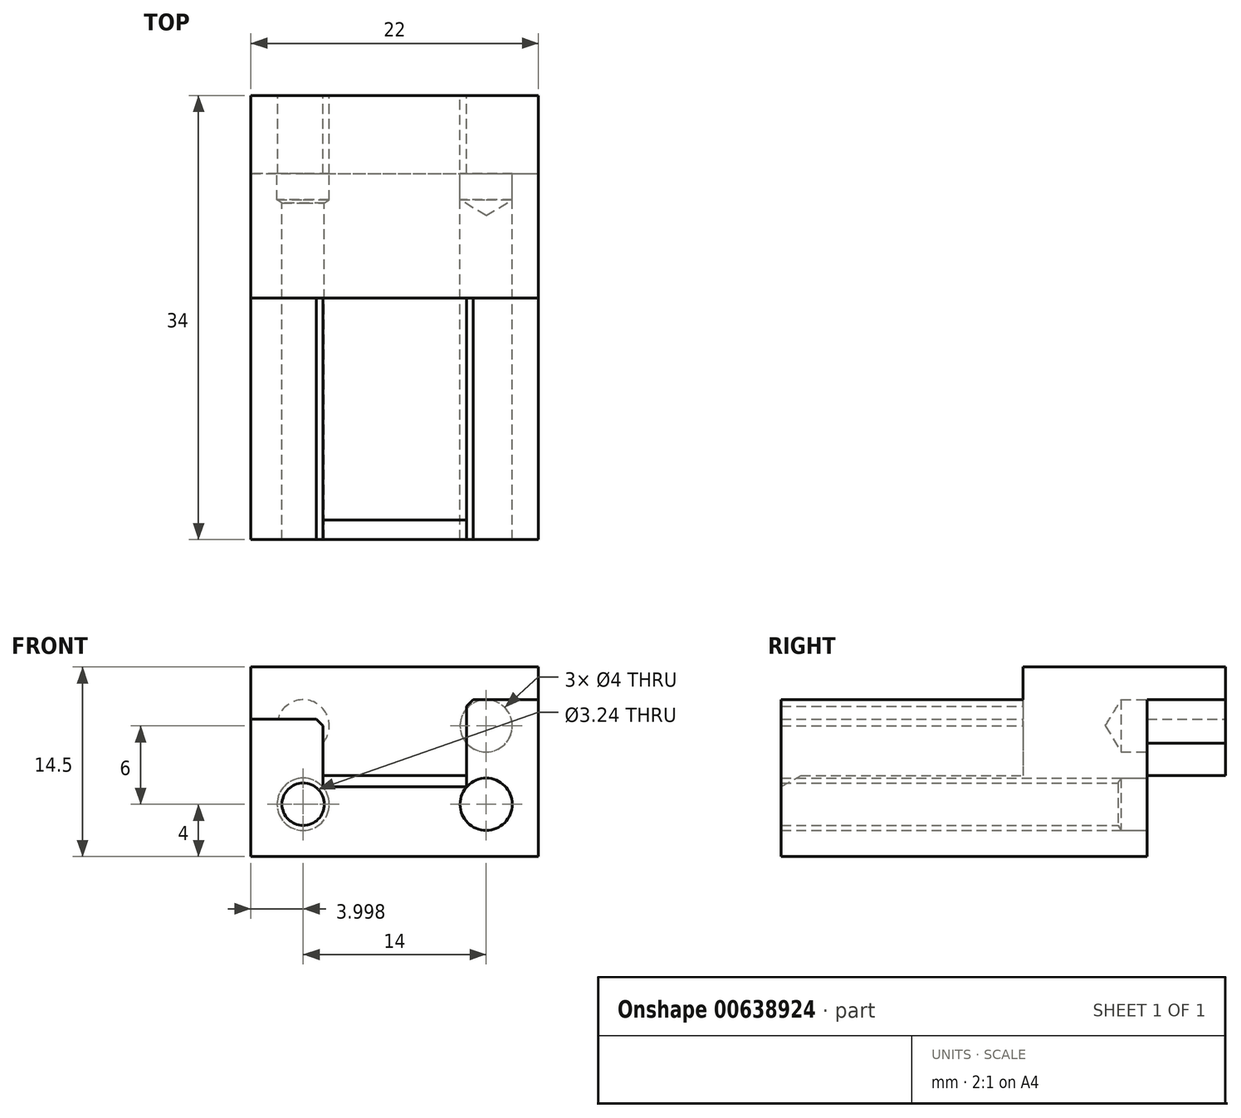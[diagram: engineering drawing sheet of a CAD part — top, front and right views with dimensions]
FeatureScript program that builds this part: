
annotation { "Feature Type Name" : "Feature", "Feature Type Description" : "" }
export const myFeature = defineFeature(function(context is Context, id is Id, definition is map)
    precondition{}
    {
        {
            var Q0;
            Q0=qCreatedBy(makeId("Front.planeOp"),FACE);
            var sketch = newSketch(context, id + "F0", { "sketchPlane" : qUnion([Q0])});
            skLineSegment(sketch, "E0", {"start": v(-38.92, -1.05) * mm, "end": v(-27.92, -1.05) * mm});
            skLineSegment(sketch, "E1", {"start": v(-44.42, 7.25) * mm, "end": v(-44.42, -7.25) * mm});
            skLineSegment(sketch, "E2", {"start": v(-27.92, 4.25) * mm, "end": v(-27.42, 4.75) * mm});
            skLineSegment(sketch, "E3", {"start": v(-38.92, 0.45) * mm, "end": v(-27.92, 0.45) * mm});
            skLineSegment(sketch, "E4", {"start": v(-39.42, 3.25) * mm, "end": v(-44.42, 3.25) * mm});
            skLineSegment(sketch, "E5", {"start": v(-38.92, 2.75) * mm, "end": v(-39.42, 3.25) * mm});
            skLineSegment(sketch, "E6", {"start": v(-27.92, 4.25) * mm, "end": v(-27.92, -1.05) * mm});
            skLineSegment(sketch, "E7", {"start": v(-38.92, 2.75) * mm, "end": v(-38.92, -1.05) * mm});
            skCircle(sketch, "E8", {"center": v(-26.42, 2.75) * mm, "radius": 1.62 * mm});
            skArc(sketch, "E9", {"start": v(-28.35, 2.23) * mm, "mid": v(-24.7, 1.75) * mm, "end": v(-26.94, 4.68) * mm});
            skCircle(sketch, "E10", {"center": v(-26.42, -3.25) * mm, "radius": 2 * mm});
            skLineSegment(sketch, "E11", {"start": v(-44.42, -7.25) * mm, "end": v(-22.42, -7.25) * mm});
            skLineSegment(sketch, "E12", {"start": v(-27.42, 4.75) * mm, "end": v(-22.42, 4.75) * mm});
            skLineSegment(sketch, "E13", {"start": v(-22.42, 7.25) * mm, "end": v(-44.42, 7.25) * mm});
            skLineSegment(sketch, "E14", {"start": v(-22.42, 7.25) * mm, "end": v(-22.42, -7.25) * mm});
            skCircle(sketch, "E15", {"center": v(-40.42, -3.25) * mm, "radius": 1.62 * mm});
            skArc(sketch, "E16", {"start": v(-39.9, -1.32) * mm, "mid": v(-42.15, -4.25) * mm, "end": v(-38.5, -3.77) * mm});
            skCircle(sketch, "E17", {"center": v(-40.42, 2.75) * mm, "radius": 2 * mm});
            skLineSegment(sketch, "E18", {"start": v(9.33, -1.05) * mm, "end": v(11.93, 0.45) * mm});
            skLineSegment(sketch, "E19", {"start": v(9.33, 3.25) * mm, "end": v(9.33, -7.25) * mm});
            skLineSegment(sketch, "E20", {"start": v(27.83, 7.25) * mm, "end": v(43.33, 7.25) * mm});
            skLineSegment(sketch, "E21", {"start": v(27.83, 7.25) * mm, "end": v(27.83, 0.45) * mm});
            skLineSegment(sketch, "E22", {"start": v(35.46, 2.75) * mm, "end": v(44.04, 2.75) * mm});
            skLineSegment(sketch, "E23", {"start": v(37.33, 4.75) * mm, "end": v(36.17, 2.75) * mm});
            skLineSegment(sketch, "E24", {"start": v(37.33, 0.75) * mm, "end": v(36.17, 2.75) * mm});
            skLineSegment(sketch, "E25", {"start": v(37.33, 0.75) * mm, "end": v(43.33, 0.75) * mm});
            skLineSegment(sketch, "E26", {"start": v(37.33, 4.75) * mm, "end": v(37.33, 0.75) * mm});
            skLineSegment(sketch, "E27", {"start": v(43.33, 4.75) * mm, "end": v(37.33, 4.75) * mm});
            skLineSegment(sketch, "E28", {"start": v(31.3, -3.25) * mm, "end": v(44.42, -3.25) * mm});
            skLineSegment(sketch, "E29", {"start": v(35.33, -1.25) * mm, "end": v(34.67, -1.63) * mm});
            skLineSegment(sketch, "E30", {"start": v(35.33, -5.25) * mm, "end": v(34.67, -4.87) * mm});
            skLineSegment(sketch, "E31", {"start": v(43.33, -1.25) * mm, "end": v(35.33, -1.25) * mm});
            skLineSegment(sketch, "E32", {"start": v(35.33, -5.25) * mm, "end": v(43.33, -5.25) * mm});
            skLineSegment(sketch, "E33", {"start": v(35.33, -1.25) * mm, "end": v(35.33, -5.25) * mm});
            skLineSegment(sketch, "E34", {"start": v(33.33, -1.63) * mm, "end": v(32.4, -3.25) * mm});
            skLineSegment(sketch, "E35", {"start": v(33.33, -4.87) * mm, "end": v(32.4, -3.25) * mm});
            skLineSegment(sketch, "E36", {"start": v(33.33, -4.87) * mm, "end": v(43.33, -4.87) * mm});
            skLineSegment(sketch, "E37", {"start": v(33.33, -1.63) * mm, "end": v(33.33, -4.87) * mm});
            skLineSegment(sketch, "E38", {"start": v(43.33, -1.63) * mm, "end": v(33.33, -1.63) * mm});
            skLineSegment(sketch, "E39", {"start": v(9.33, -7.25) * mm, "end": v(43.33, -7.25) * mm});
            skLineSegment(sketch, "E40", {"start": v(11.93, 0.45) * mm, "end": v(27.83, 0.45) * mm});
            skLineSegment(sketch, "E41", {"start": v(9.33, 3.25) * mm, "end": v(27.83, 3.25) * mm});
            skLineSegment(sketch, "E42", {"start": v(43.33, -7.25) * mm, "end": v(43.33, 7.25) * mm});
            skSolve(sketch);
        }
        {
            var Q0;
            {var subQ0=sQuery(id+"F0.wireOp",EDGE,"E0");Q0=makeQuery(id+"F0.imprint","IMPRINT",FACE,{"disambiguationData":[TD([[makeQuery(id+"F0.imprint","IMPRINT",EDGE,{"derivedFrom":subQ0}),1.0]])]});}
            var Q1;
            {var subQ0=sQuery(id+"F0.wireOp",EDGE,"E5");Q1=makeQuery(id+"F0.imprint","IMPRINT",FACE,{"disambiguationData":[TD([[makeQuery(id+"F0.imprint","IMPRINT",EDGE,{"derivedFrom":subQ0}),1.0]])]});}
            var Q2;
            {var subQ8=sQuery(id+"F0.wireOp",EDGE,"E2");Q2=makeQuery(id+"F0.imprint","IMPRINT",FACE,{"disambiguationData":[TD([[makeQuery(id+"F0.imprint","IMPRINT",EDGE,{"derivedFrom":subQ8}),1.0]])]});}
            var Q3;
            {var subQ0=sQuery(id+"F0.wireOp",EDGE,"E5");Q3=makeQuery(id+"F0.imprint","IMPRINT",FACE,{"disambiguationData":[TD([[makeQuery(id+"F0.imprint","IMPRINT",EDGE,{"derivedFrom":subQ0}),-1.0]])]});}
            var Q4;
            {var subQ0=sQuery(id+"F0.wireOp",EDGE,"E8");var subQ1=sQuery(id+"F0.wireOp",EDGE,"E6");var subQ2=makeQuery(id+"F0.imprint","INTERSECT",VERTEX,{"disambiguationData":[OD(0.0)],"derivedFrom":[subQ1,subQ0]});Q4=makeQuery(id+"F0.imprint","IMPRINT",FACE,{"disambiguationData":[TD([[makeQuery(id+"F0.imprint","IMPRINT",EDGE,{"disambiguationData":[TD([[subQ2,-1.0]])],"derivedFrom":subQ1}),1.0]])]});}
            var Q5;
            {var subQ7=sQuery(id+"F0.wireOp",EDGE,"E0");Q5=makeQuery(id+"F0.imprint","IMPRINT",FACE,{"disambiguationData":[TD([[makeQuery(id+"F0.imprint","IMPRINT",EDGE,{"derivedFrom":subQ7}),-1.0]])]});}
            var Q6;
            Q6=makeQuery(id+"F0.imprint","IMPRINT",FACE,{"disambiguationData":[TD([[makeQuery(id+"F0.imprint","IMPRINT",EDGE,{"derivedFrom":sQuery(id+"F0.wireOp",EDGE,"E10")}),-1.0]])]});
            var Q7;
            Q7=makeQuery(id+"F0.imprint","IMPRINT",FACE,{"disambiguationData":[TD([[makeQuery(id+"F0.imprint","IMPRINT",EDGE,{"derivedFrom":sQuery(id+"F0.wireOp",EDGE,"E15")}),-1.0]])]});
            var Q8;
            {var subQ7=sQuery(id+"F0.wireOp",EDGE,"E2");Q8=makeQuery(id+"F0.imprint","IMPRINT",FACE,{"disambiguationData":[TD([[makeQuery(id+"F0.imprint","IMPRINT",EDGE,{"derivedFrom":subQ7}),-1.0]])]});}
            var Q9;
            {var subQ0=sQuery(id+"F0.wireOp",EDGE,"E8");var subQ1=sQuery(id+"F0.wireOp",EDGE,"E6");var subQ2=makeQuery(id+"F0.imprint","INTERSECT",VERTEX,{"disambiguationData":[OD(0.0)],"derivedFrom":[subQ1,subQ0]});Q9=makeQuery(id+"F0.imprint","IMPRINT",FACE,{"disambiguationData":[TD([[makeQuery(id+"F0.imprint","IMPRINT",EDGE,{"disambiguationData":[TD([[subQ2,-1.0]])],"derivedFrom":subQ1}),-1.0]])]});}
            extrude(context, id + "F1", {"entities" : qUnion([Q0, Q1, Q2, Q3, Q4, Q5, Q6, Q7, Q8, Q9]), "depth" : 15.5 * mm, "offsetDistance" : 25 * mm});
        }
        {
            var Q0;
            Q0=makeQuery(id+"F1.opExtrude","CAP_FACE",FACE,{"disambiguationData":[OSD([sQuery(id+"F0.wireOp",EDGE,"E1"),sQuery(id+"F0.wireOp",EDGE,"E11"),sQuery(id+"F0.wireOp",EDGE,"E13"),sQuery(id+"F0.wireOp",EDGE,"E14")])],"isStart":false});
            var sketch = newSketch(context, id + "F2", { "sketchPlane" : qUnion([Q0])});
            skLineSegment(sketch, "E43.0", {"start": v(-38.92, -1.05) * mm, "end": v(-27.92, -1.05) * mm});
            skPoint(sketch, "E44.0", {"position": v(-39.17, 3) * mm});
            skLineSegment(sketch, "E45.0", {"start": v(-39.42, 3.25) * mm, "end": v(-44.42, 3.25) * mm});
            skLineSegment(sketch, "E46.0", {"start": v(-38.92, 2.75) * mm, "end": v(-39.42, 3.25) * mm});
            skLineSegment(sketch, "E47.0", {"start": v(-38.92, 2.75) * mm, "end": v(-38.92, -1.05) * mm});
            skLineSegment(sketch, "E48.0", {"start": v(-27.92, 4.25) * mm, "end": v(-27.92, -1.05) * mm});
            skLineSegment(sketch, "E49.0", {"start": v(-27.92, 4.25) * mm, "end": v(-27.42, 4.75) * mm});
            skLineSegment(sketch, "E50.0", {"start": v(-27.42, 4.75) * mm, "end": v(-22.42, 4.75) * mm});
            skLineSegment(sketch, "E51.0", {"start": v(-22.42, 7.25) * mm, "end": v(-22.42, -7.25) * mm});
            skLineSegment(sketch, "E52.0", {"start": v(-44.42, 7.25) * mm, "end": v(-44.42, -7.25) * mm});
            skLineSegment(sketch, "E53.0", {"start": v(-44.42, -7.25) * mm, "end": v(-22.42, -7.25) * mm});
            skSolve(sketch);
        }
        {
            var Q0;
            Q0=makeQuery(id+"F2.imprint","IMPRINT",FACE,{"disambiguationData":[TD([[makeQuery(id+"F2.imprint","IMPRINT",EDGE,{"derivedFrom":sQuery(id+"F2.wireOp",EDGE,"E43.0")}),-1.0]])]});
            extrude(context, id + "F3", {"entities" : qUnion([Q0]), "operationType" : NewBodyOperationType.ADD, "depth" : 18.5 * mm, "offsetDistance" : 25 * mm});
        }
        {
            var Q0;
            Q0=sQuery(id+"F0.wireOp",VERTEX,"E15.center");
            var Q1;
            Q1=sQuery(id+"F0.wireOp",VERTEX,"E8.center");
            var Q2;
            Q2=makeQuery(id+"F1.opExtrude","SWEPT_BODY",BODY,{"disambiguationData":[OSD([sQuery(id+"F0.wireOp",EDGE,"E1"),sQuery(id+"F0.wireOp",EDGE,"E11"),sQuery(id+"F0.wireOp",EDGE,"E13"),sQuery(id+"F0.wireOp",EDGE,"E14")])]});
            hole(context, id + "F4", {"style" : HoleStyle.SIMPLE, "endStyle" : HoleEndStyle.BLIND, "oppositeDirection" : true, "holeDiameter" : 4 * mm, "majorDiameter" : 5 * mm, "holeDepth" : 8 * mm, "isTappedThrough" : true, "tappedDepth" : 12 * mm, "tapClearance" : 3, "locations" : qUnion([Q0, Q1]), "scope" : qUnion([Q2])});
        }
        {
            var Q0;
            {var subQ0=sQuery(id+"F0.wireOp",EDGE,"E5");Q0=makeQuery(id+"F0.imprint","IMPRINT",FACE,{"disambiguationData":[TD([[makeQuery(id+"F0.imprint","IMPRINT",EDGE,{"derivedFrom":subQ0}),-1.0]])]});}
            var Q1;
            {var subQ0=sQuery(id+"F0.wireOp",EDGE,"E5");Q1=makeQuery(id+"F0.imprint","IMPRINT",FACE,{"disambiguationData":[TD([[makeQuery(id+"F0.imprint","IMPRINT",EDGE,{"derivedFrom":subQ0}),1.0]])]});}
            var Q2;
            Q2=makeQuery(id+"F0.imprint","IMPRINT",FACE,{"disambiguationData":[TD([[makeQuery(id+"F0.imprint","IMPRINT",EDGE,{"derivedFrom":sQuery(id+"F0.wireOp",EDGE,"E10")}),-1.0]])]});
            extrude(context, id + "F5", {"entities" : qUnion([Q0, Q1, Q2]), "operationType" : NewBodyOperationType.REMOVE, "depth" : 6 * mm, "offsetDistance" : 25 * mm});
        }
        {
            var Q0;
            Q0=makeQuery(id+"F3.opExtrude","CAP_EDGE",EDGE,{"disambiguationData":[OSD([sQuery(id+"F2.wireOp",EDGE,"E43.0")])],"isStart":false});
            chamfer(context, id + "F6", {"entities" : qUnion([Q0]), "chamferType" : ChamferType.OFFSET_ANGLE, "width" : 1.5 * mm, "oppositeDirection" : false, "angle" : 30 * degree, "tangentPropagation" : true});
        }
    });
